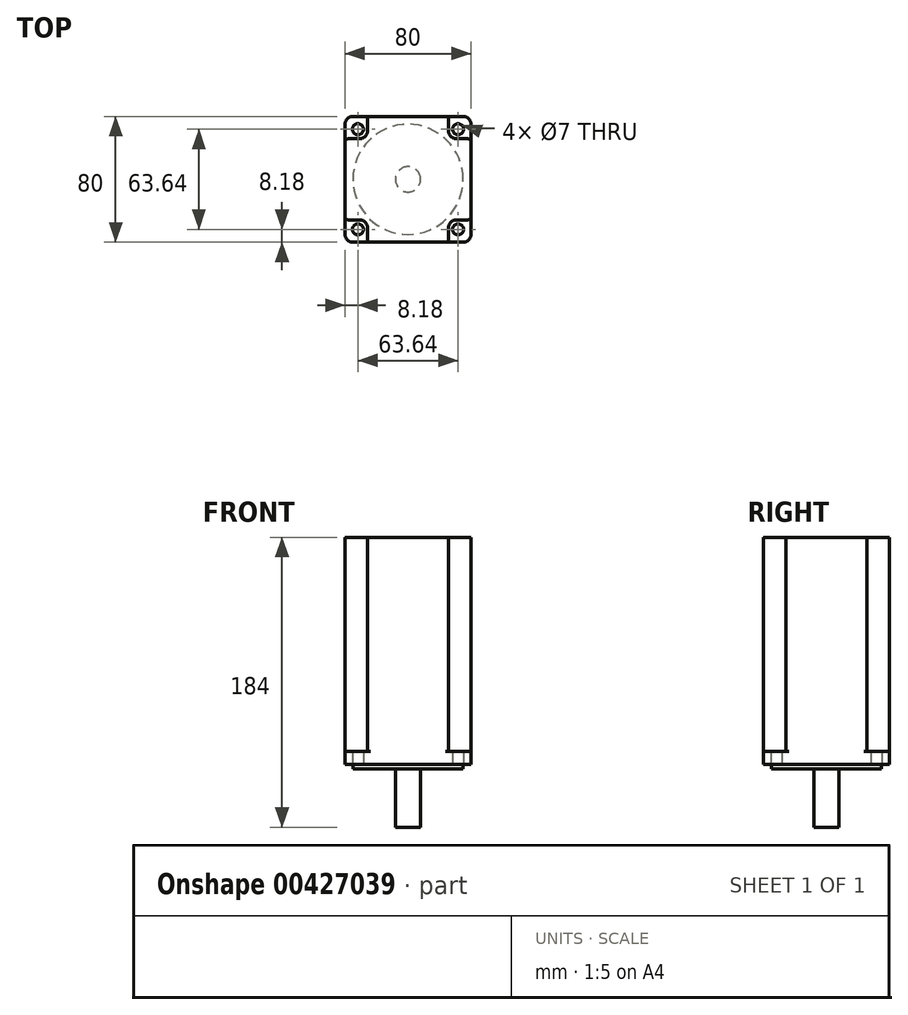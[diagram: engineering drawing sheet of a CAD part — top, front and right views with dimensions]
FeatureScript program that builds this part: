
annotation { "Feature Type Name" : "Feature", "Feature Type Description" : "" }
export const myFeature = defineFeature(function(context is Context, id is Id, definition is map)
    precondition{}
    {
        {
            var Q0;
            Q0=qCreatedBy(makeId("Top.planeOp"),FACE);
            var sketch = newSketch(context, id + "F0", { "sketchPlane" : qUnion([Q0])});
            skLineSegment(sketch, "E0.bottom", {"start": v(-35, 40) * mm, "end": v(35, 40) * mm});
            skLineSegment(sketch, "E0.top", {"start": v(-35, -40) * mm, "end": v(35, -40) * mm});
            skLineSegment(sketch, "E0.left", {"start": v(-40, 35) * mm, "end": v(-40, -35) * mm});
            skLineSegment(sketch, "E0.right", {"start": v(40, 35) * mm, "end": v(40, -35) * mm});
            skCircle(sketch, "E1", {"center": v(0, 0) * mm, "radius": 45 * mm});
            skCircle(sketch, "E2", {"center": v(-31.82, 31.82) * mm, "radius": 3.5 * mm});
            skCircle(sketch, "E3", {"center": v(31.82, 31.82) * mm, "radius": 3.5 * mm});
            skCircle(sketch, "E4", {"center": v(31.82, -31.82) * mm, "radius": 3.5 * mm});
            skCircle(sketch, "E5", {"center": v(-31.82, -31.82) * mm, "radius": 3.5 * mm});
            skLineSegment(sketch, "E6", {"start": v(-31.82, 31.82) * mm, "end": v(31.82, 31.82) * mm});
            skLineSegment(sketch, "E7", {"start": v(-31.82, 31.82) * mm, "end": v(-31.82, -31.82) * mm});
            skPoint(sketch, "E8.visualSharp", {"position": v(-40, 40) * mm});
            skArc(sketch, "E8.filletArc", {"start": v(-35, 40) * mm, "mid": v(-38.54, 38.54) * mm, "end": v(-40, 35) * mm});
            skPoint(sketch, "E9.visualSharp", {"position": v(40, 40) * mm});
            skArc(sketch, "E9.filletArc", {"start": v(40, 35) * mm, "mid": v(38.54, 38.54) * mm, "end": v(35, 40) * mm});
            skPoint(sketch, "E10.visualSharp", {"position": v(40, -40) * mm});
            skArc(sketch, "E10.filletArc", {"start": v(35, -40) * mm, "mid": v(38.54, -38.54) * mm, "end": v(40, -35) * mm});
            skPoint(sketch, "E11.visualSharp", {"position": v(-40, -40) * mm});
            skArc(sketch, "E11.filletArc", {"start": v(-40, -35) * mm, "mid": v(-38.54, -38.54) * mm, "end": v(-35, -40) * mm});
            skSolve(sketch);
        }
        {
            var Q0;
            {var subQ5=sQuery(id+"F0.wireOp",EDGE,"E8.filletArc");Q0=makeQuery(id+"F0.imprint","IMPRINT",FACE,{"disambiguationData":[TD([[makeQuery(id+"F0.imprint","IMPRINT",EDGE,{"derivedFrom":subQ5}),1.0]])]});}
            var Q1;
            {var subQ1=sQuery(id+"F0.wireOp",EDGE,"E1");var subQ5=sQuery(id+"F0.wireOp",EDGE,"E0.left");var subQ9=makeQuery(id+"F0.imprint","INTERSECT",VERTEX,{"disambiguationData":[OD(0.0)],"derivedFrom":[subQ5,subQ1]});Q1=makeQuery(id+"F0.imprint","IMPRINT",FACE,{"disambiguationData":[TD([[makeQuery(id+"F0.imprint","IMPRINT",EDGE,{"disambiguationData":[TD([[subQ9,-1.0]])],"derivedFrom":subQ5}),1.0]])]});}
            var Q2;
            {var subQ1=sQuery(id+"F0.wireOp",EDGE,"E1");var subQ10=sQuery(id+"F0.wireOp",EDGE,"E0.top");var subQ12=makeQuery(id+"F0.imprint","INTERSECT",VERTEX,{"disambiguationData":[OD(0.0)],"derivedFrom":[subQ10,subQ1]});Q2=makeQuery(id+"F0.imprint","IMPRINT",FACE,{"disambiguationData":[TD([[makeQuery(id+"F0.imprint","IMPRINT",EDGE,{"disambiguationData":[TD([[subQ12,-1.0]])],"derivedFrom":subQ10}),1.0]])]});}
            var Q3;
            {var subQ0=sQuery(id+"F0.wireOp",EDGE,"E1");var subQ1=sQuery(id+"F0.wireOp",EDGE,"E0.bottom");var subQ2=makeQuery(id+"F0.imprint","INTERSECT",VERTEX,{"disambiguationData":[OD(0.0)],"derivedFrom":[subQ1,subQ0]});Q3=makeQuery(id+"F0.imprint","IMPRINT",FACE,{"disambiguationData":[TD([[makeQuery(id+"F0.imprint","IMPRINT",EDGE,{"disambiguationData":[TD([[subQ2,-1.0]])],"derivedFrom":subQ1}),-1.0]])]});}
            var Q4;
            {var subQ6=sQuery(id+"F0.wireOp",EDGE,"E9.filletArc");Q4=makeQuery(id+"F0.imprint","IMPRINT",FACE,{"disambiguationData":[TD([[makeQuery(id+"F0.imprint","IMPRINT",EDGE,{"derivedFrom":subQ6}),1.0]])]});}
            var Q5;
            {var subQ5=sQuery(id+"F0.wireOp",EDGE,"E11.filletArc");Q5=makeQuery(id+"F0.imprint","IMPRINT",FACE,{"disambiguationData":[TD([[makeQuery(id+"F0.imprint","IMPRINT",EDGE,{"derivedFrom":subQ5}),1.0]])]});}
            var Q6;
            {var subQ5=sQuery(id+"F0.wireOp",EDGE,"E10.filletArc");Q6=makeQuery(id+"F0.imprint","IMPRINT",FACE,{"disambiguationData":[TD([[makeQuery(id+"F0.imprint","IMPRINT",EDGE,{"derivedFrom":subQ5}),1.0]])]});}
            extrude(context, id + "F1", {"entities" : qUnion([Q0, Q1, Q2, Q3, Q4, Q5, Q6]), "depth" : 8 * mm});
        }
        {
            var Q0;
            Q0=makeQuery(id+"F1.opExtrude","CAP_FACE",FACE,{"disambiguationData":[OSD([sQuery(id+"F0.wireOp",EDGE,"E0.bottom"),sQuery(id+"F0.wireOp",EDGE,"E0.top"),sQuery(id+"F0.wireOp",EDGE,"E0.left"),sQuery(id+"F0.wireOp",EDGE,"E0.right"),sQuery(id+"F0.wireOp",EDGE,"E2"),sQuery(id+"F0.wireOp",EDGE,"E3"),sQuery(id+"F0.wireOp",EDGE,"E4"),sQuery(id+"F0.wireOp",EDGE,"E5"),sQuery(id+"F0.wireOp",EDGE,"E8.filletArc"),sQuery(id+"F0.wireOp",EDGE,"E9.filletArc"),sQuery(id+"F0.wireOp",EDGE,"E10.filletArc"),sQuery(id+"F0.wireOp",EDGE,"E11.filletArc")])],"isStart":true});
            var sketch = newSketch(context, id + "F2", { "sketchPlane" : qUnion([Q0])});
            skCircle(sketch, "E12", {"center": v(0, 0) * mm, "radius": 35 * mm});
            skSolve(sketch);
        }
        {
            var Q0;
            Q0=makeQuery(id+"F2.imprint","IMPRINT",FACE,{"disambiguationData":[TD([[makeQuery(id+"F2.imprint","IMPRINT",EDGE,{"derivedFrom":sQuery(id+"F2.wireOp",EDGE,"E12")}),1.0]])]});
            var Q1;
            Q1=makeQuery(id+"F2.imprint","IMPRINT",FACE,{"disambiguationData":[TD([[makeQuery(id+"F2.imprint","IMPRINT",EDGE,{"derivedFrom":sQuery(id+"F2.wireOp",EDGE,"aQVRXsAJ-xXH7-UplE-mY1b-cshlsRrdaRUK")}),1.0]])]});
            extrude(context, id + "F3", {"entities" : qUnion([Q0, Q1]), "operationType" : NewBodyOperationType.ADD, "depth" : 3 * mm});
        }
        {
            var Q0;
            Q0=makeQuery(id+"F3.opExtrude","CAP_FACE",FACE,{"disambiguationData":[OSD([sQuery(id+"F2.wireOp",EDGE,"E12")])],"isStart":false});
            var sketch = newSketch(context, id + "F4", { "sketchPlane" : qUnion([Q0])});
            skCircle(sketch, "E13", {"center": v(0, 0) * mm, "radius": 8 * mm});
            skSolve(sketch);
        }
        {
            var Q0;
            Q0=makeQuery(id+"F4.imprint","IMPRINT",FACE,{"disambiguationData":[TD([[makeQuery(id+"F4.imprint","IMPRINT",EDGE,{"derivedFrom":sQuery(id+"F4.wireOp",EDGE,"E13")}),1.0]])]});
            extrude(context, id + "F5", {"entities" : qUnion([Q0]), "operationType" : NewBodyOperationType.ADD, "depth" : 37 * mm});
        }
        {
            var Q0;
            Q0=makeQuery(id+"F1.opExtrude","CAP_FACE",FACE,{"disambiguationData":[OSD([sQuery(id+"F0.wireOp",EDGE,"E0.bottom"),sQuery(id+"F0.wireOp",EDGE,"E0.top"),sQuery(id+"F0.wireOp",EDGE,"E0.left"),sQuery(id+"F0.wireOp",EDGE,"E0.right"),sQuery(id+"F0.wireOp",EDGE,"E2"),sQuery(id+"F0.wireOp",EDGE,"E3"),sQuery(id+"F0.wireOp",EDGE,"E4"),sQuery(id+"F0.wireOp",EDGE,"E5"),sQuery(id+"F0.wireOp",EDGE,"E8.filletArc"),sQuery(id+"F0.wireOp",EDGE,"E9.filletArc"),sQuery(id+"F0.wireOp",EDGE,"E10.filletArc"),sQuery(id+"F0.wireOp",EDGE,"E11.filletArc")])],"isStart":false});
            var sketch = newSketch(context, id + "F6", { "sketchPlane" : qUnion([Q0])});
            skLineSegment(sketch, "E14", {"start": v(-38, 25.75) * mm, "end": v(-30.75, 25.75) * mm});
            skLineSegment(sketch, "E15", {"start": v(-25.75, 30.75) * mm, "end": v(-25.75, 38) * mm});
            skLineSegment(sketch, "E16", {"start": v(-23.75, 40) * mm, "end": v(23.75, 40) * mm});
            skLineSegment(sketch, "E17", {"start": v(25.75, 38) * mm, "end": v(25.75, 30.75) * mm});
            skLineSegment(sketch, "E18", {"start": v(30.75, 25.75) * mm, "end": v(38, 25.75) * mm});
            skLineSegment(sketch, "E19", {"start": v(40, 23.75) * mm, "end": v(40, -23.75) * mm});
            skLineSegment(sketch, "E20", {"start": v(38, -25.75) * mm, "end": v(30.75, -25.75) * mm});
            skLineSegment(sketch, "E21", {"start": v(25.75, -30.75) * mm, "end": v(25.75, -38) * mm});
            skLineSegment(sketch, "E22", {"start": v(23.75, -40) * mm, "end": v(-23.75, -40) * mm});
            skLineSegment(sketch, "E23", {"start": v(-25.75, -38) * mm, "end": v(-25.75, -30.75) * mm});
            skLineSegment(sketch, "E24", {"start": v(-30.75, -25.75) * mm, "end": v(-38, -25.75) * mm});
            skLineSegment(sketch, "E25", {"start": v(-40, -23.75) * mm, "end": v(-40, 23.75) * mm});
            skPoint(sketch, "E26.visualSharp", {"position": v(-25.75, 25.75) * mm});
            skArc(sketch, "E26.filletArc", {"start": v(-30.75, 25.75) * mm, "mid": v(-27.21, 27.21) * mm, "end": v(-25.75, 30.75) * mm});
            skPoint(sketch, "E27.visualSharp", {"position": v(25.75, 25.75) * mm});
            skArc(sketch, "E27.filletArc", {"start": v(25.75, 30.75) * mm, "mid": v(27.21, 27.21) * mm, "end": v(30.75, 25.75) * mm});
            skPoint(sketch, "E28.visualSharp", {"position": v(25.75, -25.75) * mm});
            skArc(sketch, "E28.filletArc", {"start": v(30.75, -25.75) * mm, "mid": v(27.21, -27.21) * mm, "end": v(25.75, -30.75) * mm});
            skPoint(sketch, "E29.visualSharp", {"position": v(-25.75, -25.75) * mm});
            skArc(sketch, "E29.filletArc", {"start": v(-25.75, -30.75) * mm, "mid": v(-27.21, -27.21) * mm, "end": v(-30.75, -25.75) * mm});
            skPoint(sketch, "E30.visualSharp", {"position": v(-40, -25.75) * mm});
            skArc(sketch, "E30.filletArc", {"start": v(-40, -23.75) * mm, "mid": v(-39.41, -25.16) * mm, "end": v(-38, -25.75) * mm});
            skPoint(sketch, "E31.visualSharp", {"position": v(-40, 25.75) * mm});
            skArc(sketch, "E31.filletArc", {"start": v(-38, 25.75) * mm, "mid": v(-39.41, 25.16) * mm, "end": v(-40, 23.75) * mm});
            skPoint(sketch, "E32.visualSharp", {"position": v(-25.75, 40) * mm});
            skArc(sketch, "E32.filletArc", {"start": v(-23.75, 40) * mm, "mid": v(-25.16, 39.41) * mm, "end": v(-25.75, 38) * mm});
            skPoint(sketch, "E33.visualSharp", {"position": v(25.75, 40) * mm});
            skArc(sketch, "E33.filletArc", {"start": v(25.75, 38) * mm, "mid": v(25.16, 39.41) * mm, "end": v(23.75, 40) * mm});
            skPoint(sketch, "E34.visualSharp", {"position": v(40, 25.75) * mm});
            skArc(sketch, "E34.filletArc", {"start": v(40, 23.75) * mm, "mid": v(39.41, 25.16) * mm, "end": v(38, 25.75) * mm});
            skPoint(sketch, "E35.visualSharp", {"position": v(40, -25.75) * mm});
            skArc(sketch, "E35.filletArc", {"start": v(38, -25.75) * mm, "mid": v(39.41, -25.16) * mm, "end": v(40, -23.75) * mm});
            skPoint(sketch, "E36.visualSharp", {"position": v(25.75, -40) * mm});
            skArc(sketch, "E36.filletArc", {"start": v(23.75, -40) * mm, "mid": v(25.16, -39.41) * mm, "end": v(25.75, -38) * mm});
            skPoint(sketch, "E37.visualSharp", {"position": v(-25.75, -40) * mm});
            skArc(sketch, "E37.filletArc", {"start": v(-25.75, -38) * mm, "mid": v(-25.16, -39.41) * mm, "end": v(-23.75, -40) * mm});
            skSolve(sketch);
        }
        {
            var Q0;
            Q0=makeQuery(id+"F6.imprint","IMPRINT",FACE,{"disambiguationData":[TD([[makeQuery(id+"F6.imprint","IMPRINT",EDGE,{"derivedFrom":sQuery(id+"F6.wireOp",EDGE,"E14")}),-1.0]])]});
            extrude(context, id + "F7", {"entities" : qUnion([Q0]), "operationType" : NewBodyOperationType.ADD, "depth" : 136 * mm});
        }
    });
